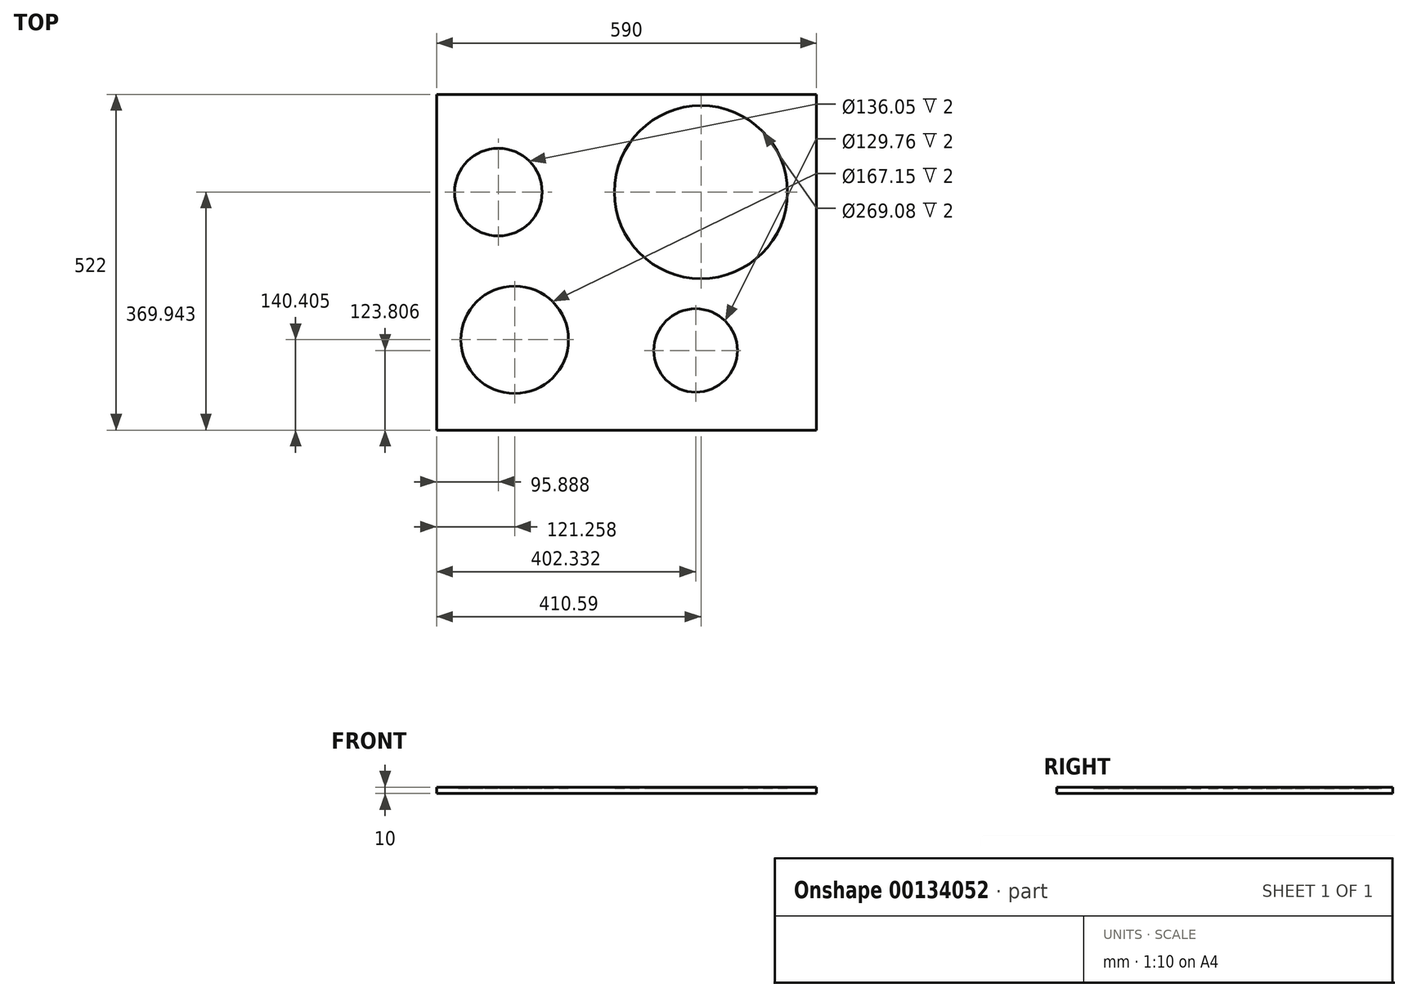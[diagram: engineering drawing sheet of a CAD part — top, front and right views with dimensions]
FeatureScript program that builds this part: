
annotation { "Feature Type Name" : "Feature", "Feature Type Description" : "" }
export const myFeature = defineFeature(function(context is Context, id is Id, definition is map)
    precondition{}
    {
        {
            var Q0;
            Q0=qCreatedBy(makeId("Top.planeOp"),FACE);
            var sketch = newSketch(context, id + "F0", { "sketchPlane" : qUnion([Q0])});
            skLineSegment(sketch, "E0.bottom", {"start": v(-42.23, 497.11) * mm, "end": v(547.77, 497.11) * mm});
            skLineSegment(sketch, "E0.top", {"start": v(-42.23, -24.89) * mm, "end": v(547.77, -24.89) * mm});
            skLineSegment(sketch, "E0.left", {"start": v(-42.23, 497.11) * mm, "end": v(-42.23, -24.89) * mm});
            skLineSegment(sketch, "E0.right", {"start": v(547.77, 497.11) * mm, "end": v(547.77, -24.89) * mm});
            skSolve(sketch);
        }
        {
            var Q0;
            Q0=makeQuery(id+"F0.imprint","IMPRINT",FACE,{"disambiguationData":[TD([[makeQuery(id+"F0.imprint","IMPRINT",EDGE,{"derivedFrom":sQuery(id+"F0.wireOp",EDGE,"E0.bottom")}),-1.0]])]});
            extrude(context, id + "F1", {"entities" : qUnion([Q0]), "depth" : 10 * mm});
        }
        {
            var Q0;
            Q0=makeQuery(id+"F1.opExtrude","CAP_FACE",FACE,{"disambiguationData":[OSD([sQuery(id+"F0.wireOp",EDGE,"E0.bottom"),sQuery(id+"F0.wireOp",EDGE,"E0.top"),sQuery(id+"F0.wireOp",EDGE,"E0.left"),sQuery(id+"F0.wireOp",EDGE,"E0.right")])],"isStart":false});
            var sketch = newSketch(context, id + "F2", { "sketchPlane" : qUnion([Q0])});
            skCircle(sketch, "E1", {"center": v(53.66, 345.05) * mm, "radius": 68.02 * mm});
            skCircle(sketch, "E2", {"center": v(368.36, 345.05) * mm, "radius": 134.54 * mm});
            skCircle(sketch, "E3", {"center": v(360.1, 98.92) * mm, "radius": 64.88 * mm});
            skCircle(sketch, "E4", {"center": v(79.03, 115.51) * mm, "radius": 83.57 * mm});
            skSolve(sketch);
        }
        {
            var Q0;
            Q0=makeQuery(id+"F2.imprint","IMPRINT",FACE,{"disambiguationData":[TD([[makeQuery(id+"F2.imprint","IMPRINT",EDGE,{"derivedFrom":sQuery(id+"F2.wireOp",EDGE,"E1")}),1.0]])]});
            var Q1;
            Q1=makeQuery(id+"F2.imprint","IMPRINT",FACE,{"disambiguationData":[TD([[makeQuery(id+"F2.imprint","IMPRINT",EDGE,{"derivedFrom":sQuery(id+"F2.wireOp",EDGE,"E2")}),1.0]])]});
            var Q2;
            Q2=makeQuery(id+"F2.imprint","IMPRINT",FACE,{"disambiguationData":[TD([[makeQuery(id+"F2.imprint","IMPRINT",EDGE,{"derivedFrom":sQuery(id+"F2.wireOp",EDGE,"E4")}),1.0]])]});
            var Q3;
            Q3=makeQuery(id+"F2.imprint","IMPRINT",FACE,{"disambiguationData":[TD([[makeQuery(id+"F2.imprint","IMPRINT",EDGE,{"derivedFrom":sQuery(id+"F2.wireOp",EDGE,"E3")}),1.0]])]});
            extrude(context, id + "F3", {"entities" : qUnion([Q0, Q1, Q2, Q3]), "operationType" : NewBodyOperationType.REMOVE, "oppositeDirection" : true, "depth" : 2 * mm});
        }
    });
